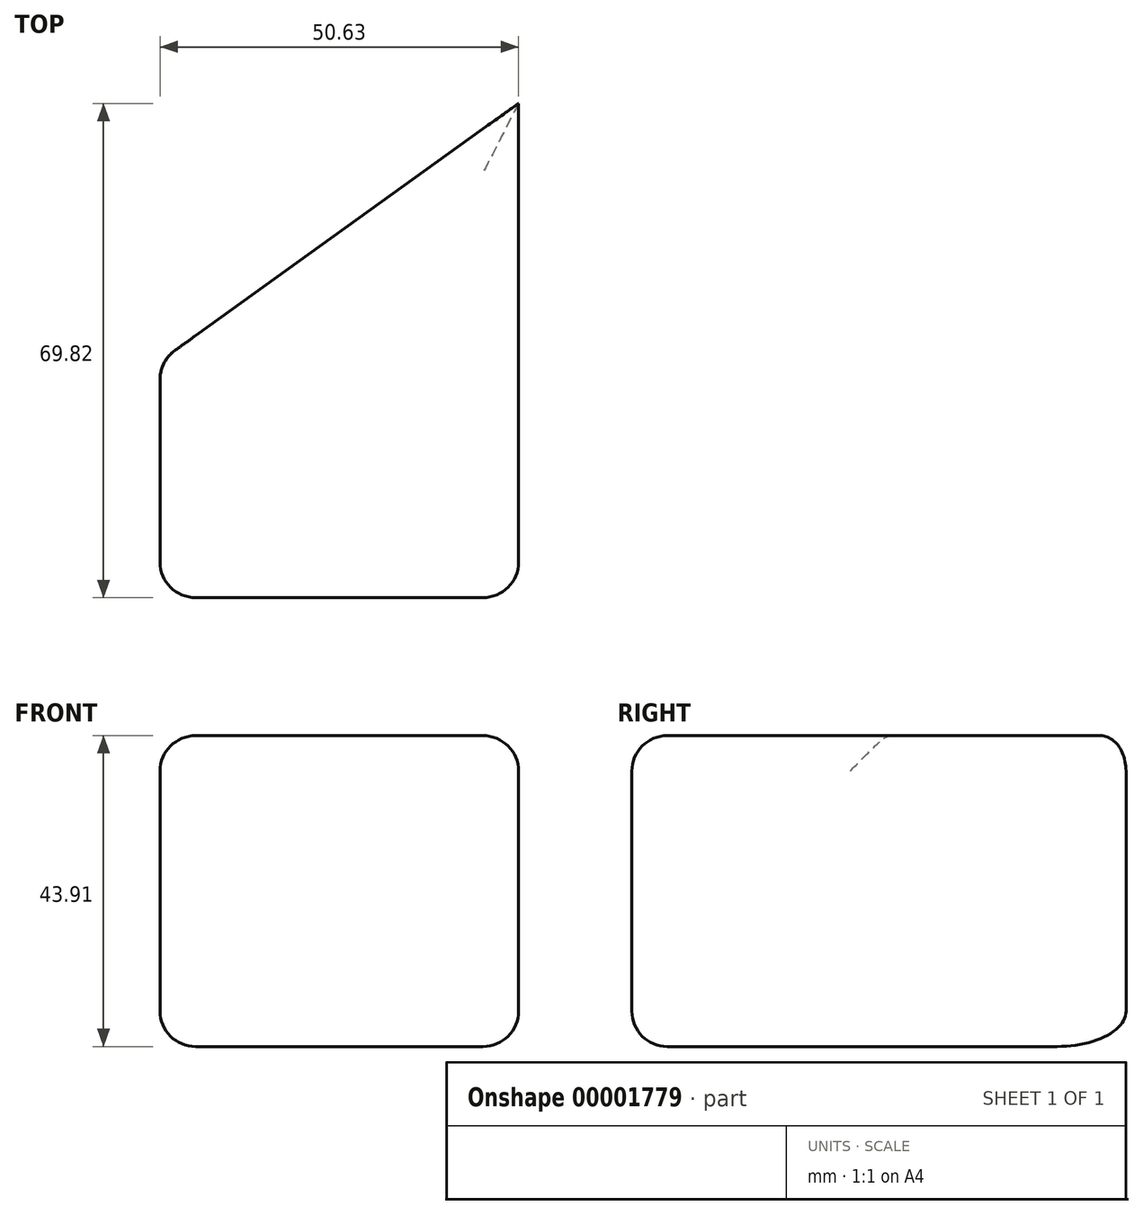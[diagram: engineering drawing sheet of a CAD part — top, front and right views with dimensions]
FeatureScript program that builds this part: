
annotation { "Feature Type Name" : "Feature", "Feature Type Description" : "" }
export const myFeature = defineFeature(function(context is Context, id is Id, definition is map)
    precondition{}
    {
        {
            var Q0;
            Q0=qCreatedBy(makeId("Top.planeOp"),FACE);
            var sketch = newSketch(context, id + "F0", { "sketchPlane" : qUnion([Q0])});
            skLineSegment(sketch, "E0", {"start": v(0, 0) * mm, "end": v(0, -33.4) * mm});
            skLineSegment(sketch, "E1", {"start": v(0, -33.4) * mm, "end": v(50.63, -33.4) * mm});
            skLineSegment(sketch, "E2", {"start": v(50.63, -33.4) * mm, "end": v(50.63, 36.42) * mm});
            skLineSegment(sketch, "E3", {"start": v(50.63, 36.42) * mm, "end": v(0, 0) * mm});
            skSolve(sketch);
        }
        {
            var Q0;
            Q0 = qSketchRegion(id + "F0", true);
            extrude(context, id + "F1", {"entities" : qUnion([Q0]), "depth" : 43.9 * mm});
        }
        {
            var Q0;
            Q0=makeQuery(id+"F1.opExtrude","SWEPT_EDGE",EDGE,{"disambiguationData":[OSD([sQuery(id+"F0.wireOp",EDGE,"E1"),sQuery(id+"F0.wireOp",EDGE,"E2")])]});
            var Q1;
            Q1=makeQuery(id+"F1.opExtrude","SWEPT_EDGE",EDGE,{"disambiguationData":[OSD([sQuery(id+"F0.wireOp",EDGE,"E0"),sQuery(id+"F0.wireOp",EDGE,"E3")])]});
            var Q2;
            Q2=makeQuery(id+"F1.opExtrude","CAP_EDGE",EDGE,{"disambiguationData":[OSD([sQuery(id+"F0.wireOp",EDGE,"E0")])],"isStart":false});
            var Q3;
            Q3=makeQuery(id+"F1.opExtrude","CAP_EDGE",EDGE,{"disambiguationData":[OSD([sQuery(id+"F0.wireOp",EDGE,"E2")])],"isStart":true});
            var Q4;
            Q4=makeQuery(id+"F1.opExtrude","CAP_EDGE",EDGE,{"disambiguationData":[OSD([sQuery(id+"F0.wireOp",EDGE,"E1")])],"isStart":false});
            var Q5;
            Q5=makeQuery(id+"F1.opExtrude","CAP_EDGE",EDGE,{"disambiguationData":[OSD([sQuery(id+"F0.wireOp",EDGE,"E2")])],"isStart":false});
            var Q6;
            Q6=makeQuery(id+"F1.opExtrude","CAP_EDGE",EDGE,{"disambiguationData":[OSD([sQuery(id+"F0.wireOp",EDGE,"E1")])],"isStart":true});
            var Q7;
            Q7=makeQuery(id+"F1.opExtrude","SWEPT_EDGE",EDGE,{"disambiguationData":[OSD([sQuery(id+"F0.wireOp",EDGE,"E0"),sQuery(id+"F0.wireOp",EDGE,"E1")])]});
            var Q8;
            Q8=makeQuery(id+"F1.opExtrude","CAP_EDGE",EDGE,{"disambiguationData":[OSD([sQuery(id+"F0.wireOp",EDGE,"E0")])],"isStart":true});
            var Q9;
            Q9=makeQuery(id+"F1.opExtrude","CAP_EDGE",EDGE,{"disambiguationData":[OSD([sQuery(id+"F0.wireOp",EDGE,"E3")])],"isStart":true});
            var Q10;
            Q10=makeQuery(id+"F1.opExtrude","SWEPT_FACE",FACE,{"disambiguationData":[OSD([sQuery(id+"F0.wireOp",EDGE,"E0")])]});
            fillet(context, id + "F2", {"entities" : qUnion([Q0, Q1, Q2, Q3, Q4, Q5, Q6, Q7, Q8, Q9, Q10]), "radius" : 5 * mm, "tangentPropagation" : true, "allowEdgeOverflow" : false});
        }
    });
